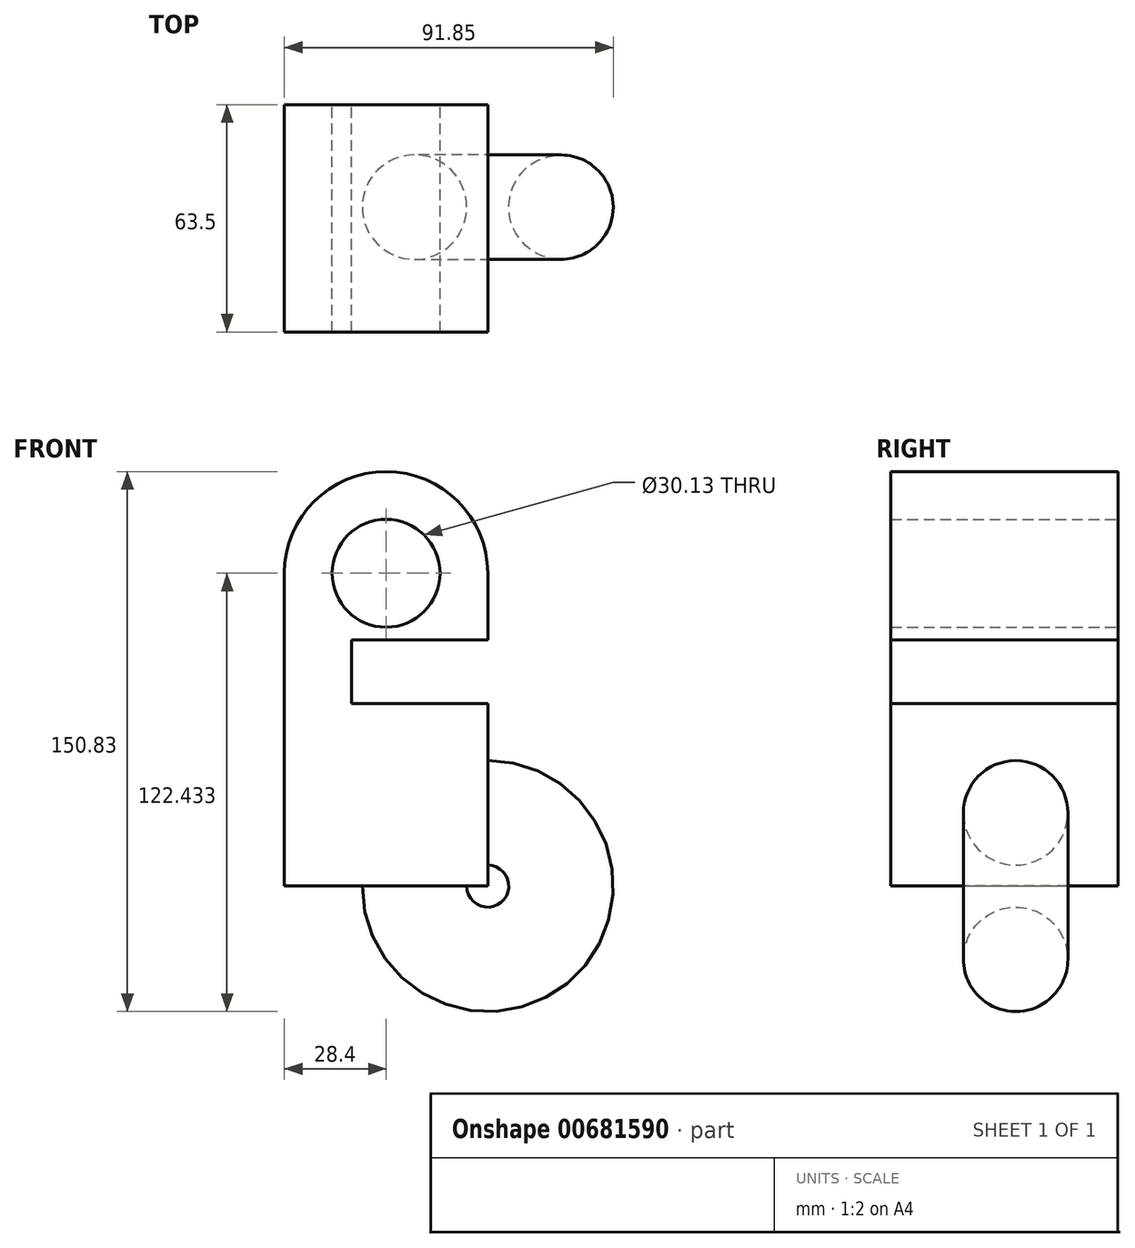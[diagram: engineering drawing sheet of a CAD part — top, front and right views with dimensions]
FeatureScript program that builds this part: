
annotation { "Feature Type Name" : "Feature", "Feature Type Description" : "" }
export const myFeature = defineFeature(function(context is Context, id is Id, definition is map)
    precondition{}
    {
        {
            var Q0;
            Q0=qCreatedBy(makeId("Front.planeOp"),FACE);
            var sketch = newSketch(context, id + "F0", { "sketchPlane" : qUnion([Q0])});
            skLineSegment(sketch, "E0.top", {"start": v(28.4, -43.7) * mm, "end": v(-28.4, -43.7) * mm});
            skLineSegment(sketch, "E0.left", {"start": v(28.4, 43.7) * mm, "end": v(28.4, -43.7) * mm});
            skLineSegment(sketch, "E0.right", {"start": v(-28.4, 43.7) * mm, "end": v(-28.4, -43.7) * mm});
            skPoint(sketch, "E0.middle", {"position": v(0, 0) * mm});
            skArc(sketch, "E1", {"start": v(28.4, 43.7) * mm, "mid": v(0, 72.1) * mm, "end": v(-28.4, 43.7) * mm});
            skCircle(sketch, "E2", {"center": v(0, 43.7) * mm, "radius": 15.06 * mm});
            skSolve(sketch);
        }
        {
            var Q0;
            Q0=makeQuery(id+"F0.imprint","IMPRINT",FACE,{"disambiguationData":[TD([[makeQuery(id+"F0.imprint","IMPRINT",EDGE,{"derivedFrom":sQuery(id+"F0.wireOp",EDGE,"E0.top")}),-1.0]])]});
            extrude(context, id + "F1", {"entities" : qUnion([Q0]), "depth" : 63.5 * mm, "offsetDistance" : 25.4 * mm});
        }
        {
            var Q0;
            Q0=makeQuery(id+"F1.opExtrude","SWEPT_FACE",FACE,{"disambiguationData":[OSD([sQuery(id+"F0.wireOp",EDGE,"E0.left")])]});
            var sketch = newSketch(context, id + "F2", { "sketchPlane" : qUnion([Q0])});
            skLineSegment(sketch, "E3", {"start": v(-63.5, 25.02) * mm, "end": v(0, 25.02) * mm});
            skLineSegment(sketch, "E4", {"start": v(-63.5, 7.28) * mm, "end": v(0, 7.28) * mm});
            skLineSegment(sketch, "E5", {"start": v(-63.5, 25.02) * mm, "end": v(-63.5, 7.28) * mm});
            skLineSegment(sketch, "E6", {"start": v(0, 25.02) * mm, "end": v(0, 7.28) * mm});
            skLineSegment(sketch, "E7", {"start": v(-63.5, 43.7) * mm, "end": v(-63.5, 25.02) * mm});
            skLineSegment(sketch, "E8", {"start": v(0, 43.7) * mm, "end": v(0, 25.02) * mm});
            skSolve(sketch);
        }
        {
            var Q0;
            Q0=makeQuery(id+"F2.imprint","IMPRINT",FACE,{"disambiguationData":[TD([[makeQuery(id+"F2.imprint","IMPRINT",EDGE,{"derivedFrom":sQuery(id+"F2.wireOp",EDGE,"E3")}),-1.0]])]});
            extrude(context, id + "F3", {"entities" : qUnion([Q0]), "operationType" : NewBodyOperationType.REMOVE, "oppositeDirection" : true, "depth" : 38.1 * mm, "offsetDistance" : 25.4 * mm});
        }
        {
            var Q0;
            {var subQ0=sQuery(id+"F0.wireOp",EDGE,"E0.top");var subQ4=sQuery(id+"F0.wireOp",EDGE,"E0.left");Q0=makeQuery(id+"F3.boolean.opBoolean","SPLIT",FACE,{"disambiguationData":[TD([makeQuery(id+"F1.opExtrude","SWEPT_FACE",FACE,{"disambiguationData":[OSD([subQ0])]})])],"derivedFrom":makeQuery(id+"F1.opExtrude","SWEPT_FACE",FACE,{"disambiguationData":[OSD([subQ4])]})});}
            var sketch = newSketch(context, id + "F4", { "sketchPlane" : qUnion([Q0])});
            skCircle(sketch, "E9", {"center": v(-28.65, -23.23) * mm, "radius": 14.6 * mm});
            skSolve(sketch);
        }
        {
            var Q0;
            Q0 = qSketchRegion(id + "F4", true);
            var Q1;
            Q1=makeQuery(id+"F1.opExtrude","SWEPT_EDGE",EDGE,{"disambiguationData":[OSD([sQuery(id+"F0.wireOp",EDGE,"E0.top"),sQuery(id+"F0.wireOp",EDGE,"E0.left")])]});
            revolve(context, id + "F5", {"operationType" : NewBodyOperationType.ADD, "entities" : qUnion([Q0]), "axis" : qUnion([Q1]), "revolveType" : RevolveType.FULL});
        }
    });
